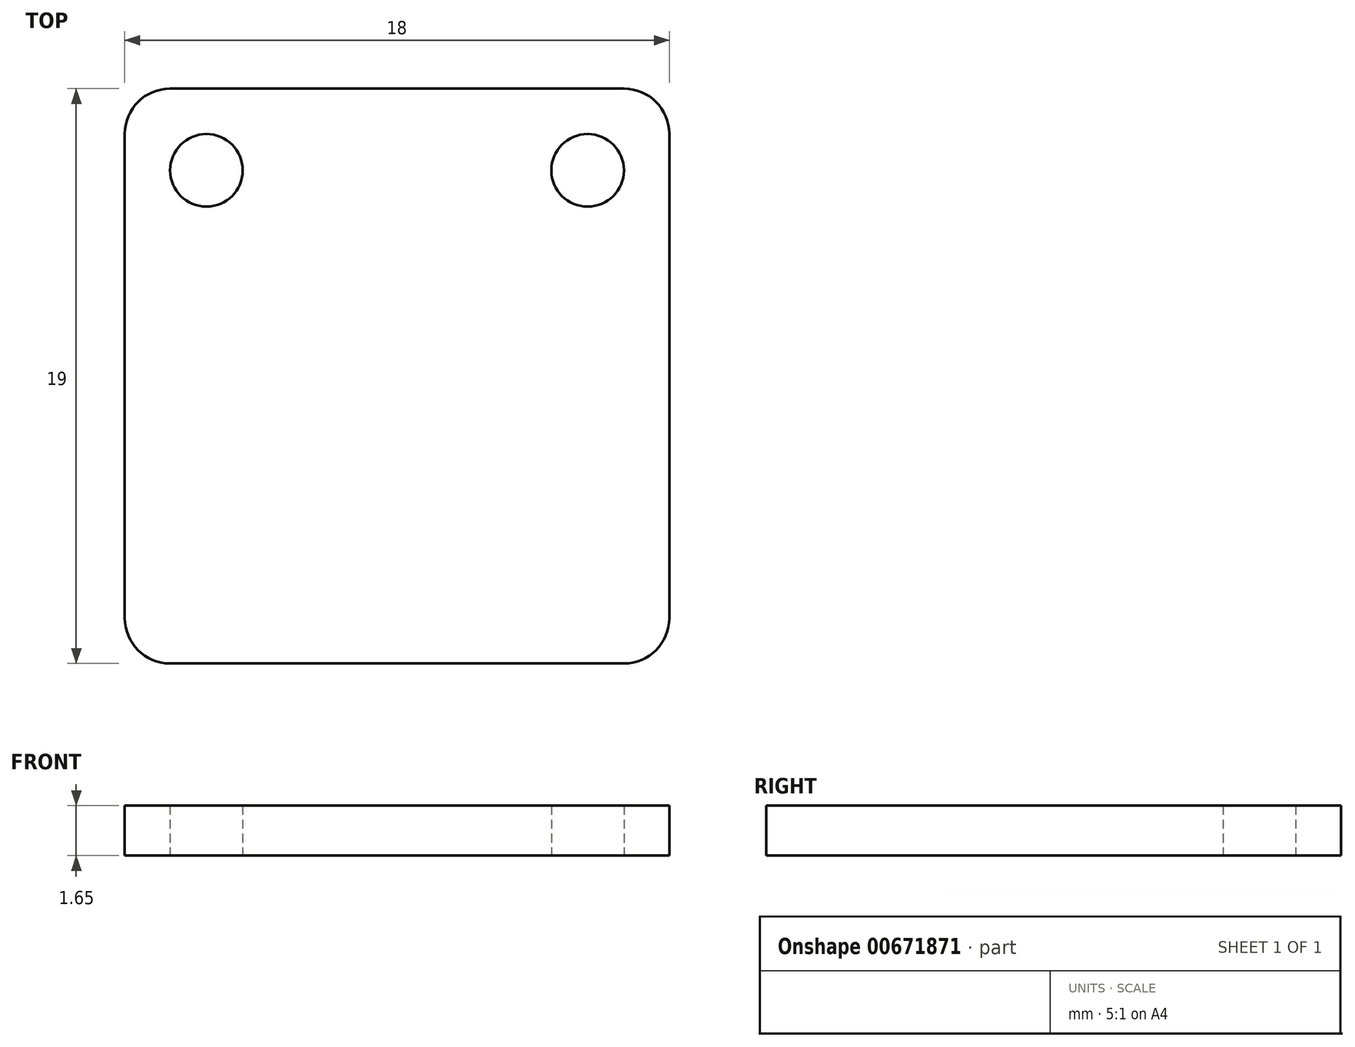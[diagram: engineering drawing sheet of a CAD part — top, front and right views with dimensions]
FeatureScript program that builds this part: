
annotation { "Feature Type Name" : "Feature", "Feature Type Description" : "" }
export const myFeature = defineFeature(function(context is Context, id is Id, definition is map)
    precondition{}
    {
        {
            var Q0;
            Q0=qCreatedBy(makeId("Top.planeOp"),FACE);
            var sketch = newSketch(context, id + "F0", { "sketchPlane" : qUnion([Q0])});
            skLineSegment(sketch, "E0.bottom", {"start": v(9, 9.5) * mm, "end": v(-9, 9.5) * mm});
            skLineSegment(sketch, "E0.top", {"start": v(9, -9.5) * mm, "end": v(-9, -9.5) * mm});
            skLineSegment(sketch, "E0.left", {"start": v(9, 9.5) * mm, "end": v(9, -9.5) * mm});
            skLineSegment(sketch, "E0.right", {"start": v(-9, 9.5) * mm, "end": v(-9, -9.5) * mm});
            skPoint(sketch, "E0.middle", {"position": v(0, 0) * mm});
            skCircle(sketch, "E1", {"center": v(-6.3, 6.8) * mm, "radius": 1.2 * mm});
            skCircle(sketch, "E2.MirrorC", {"center": v(6.3, 6.8) * mm, "radius": 1.2 * mm});
            skSolve(sketch);
        }
        {
            var Q0;
            Q0=makeQuery(id+"F0.imprint","IMPRINT",FACE,{"disambiguationData":[TD([[makeQuery(id+"F0.imprint","IMPRINT",EDGE,{"derivedFrom":sQuery(id+"F0.wireOp",EDGE,"E0.bottom")}),1.0]])]});
            extrude(context, id + "F1", {"entities" : qUnion([Q0]), "depth" : 1.65 * mm, "offsetDistance" : 25 * mm});
        }
        {
            var Q0;
            Q0=makeQuery(id+"F1.opExtrude","SWEPT_EDGE",EDGE,{"disambiguationData":[OSD([sQuery(id+"F0.wireOp",EDGE,"E0.top"),sQuery(id+"F0.wireOp",EDGE,"E0.right")])]});
            var Q1;
            Q1=makeQuery(id+"F1.opExtrude","SWEPT_EDGE",EDGE,{"disambiguationData":[OSD([sQuery(id+"F0.wireOp",EDGE,"E0.top"),sQuery(id+"F0.wireOp",EDGE,"E0.left")])]});
            var Q2;
            Q2=makeQuery(id+"F1.opExtrude","SWEPT_EDGE",EDGE,{"disambiguationData":[OSD([sQuery(id+"F0.wireOp",EDGE,"E0.bottom"),sQuery(id+"F0.wireOp",EDGE,"E0.left")])]});
            var Q3;
            Q3=makeQuery(id+"F1.opExtrude","SWEPT_EDGE",EDGE,{"disambiguationData":[OSD([sQuery(id+"F0.wireOp",EDGE,"E0.bottom"),sQuery(id+"F0.wireOp",EDGE,"E0.right")])]});
            fillet(context, id + "F2", {"entities" : qUnion([Q0, Q1, Q2, Q3]), "radius" : 1.5 * mm, "tangentPropagation" : true, "allowEdgeOverflow" : false});
        }
    });
